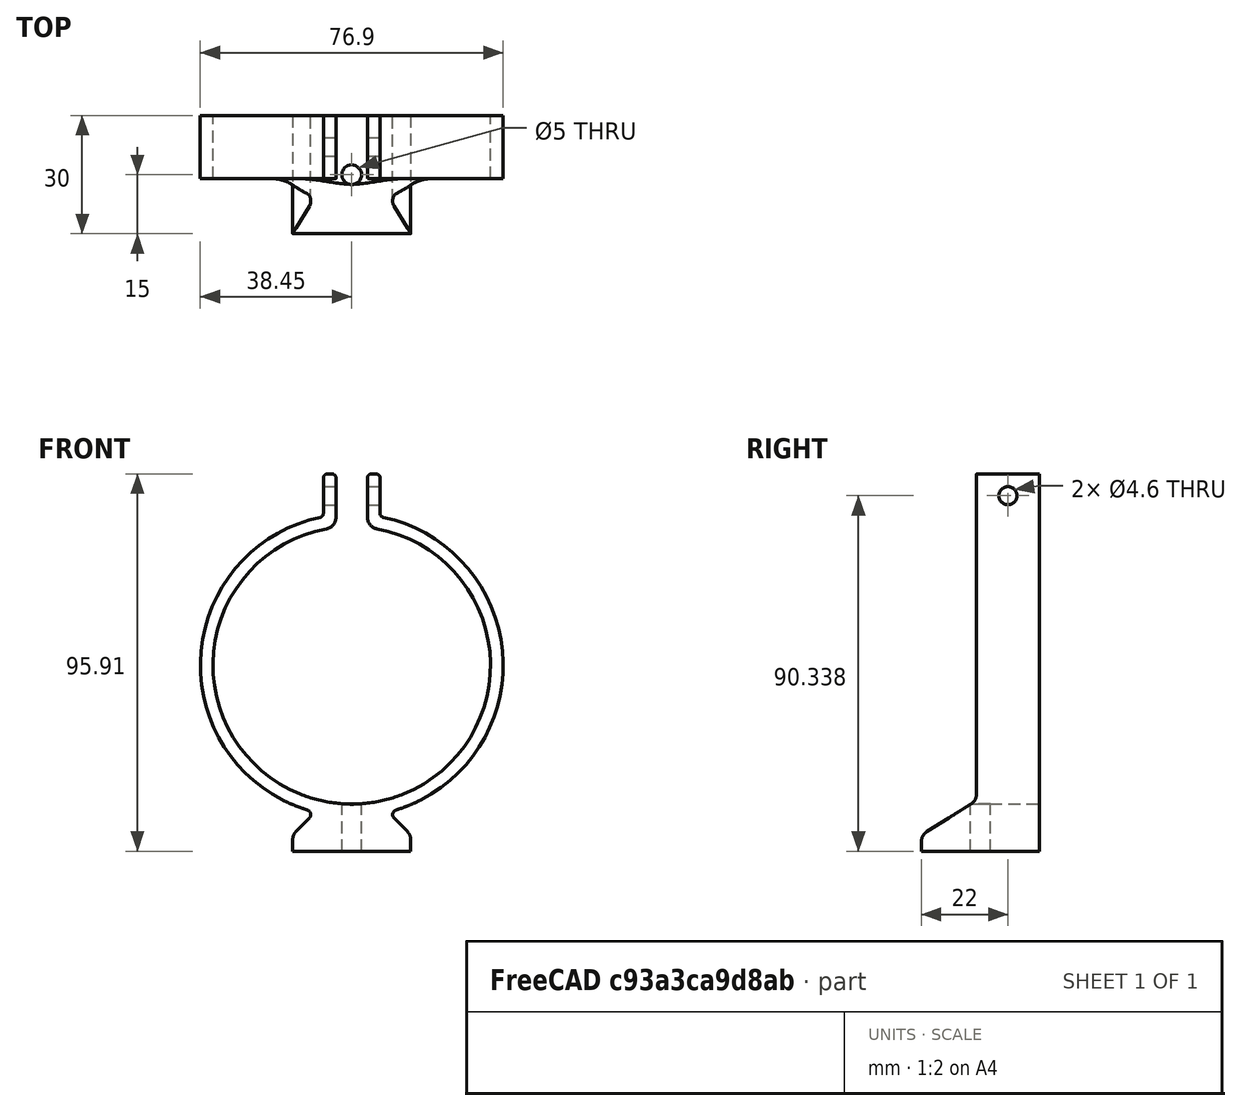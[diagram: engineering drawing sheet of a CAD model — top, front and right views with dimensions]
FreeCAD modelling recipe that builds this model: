
FCSTD DOCUMENT  (FreeCAD 1.0R39109 (Git))
Label: cam_lens_mt_v2
License: All rights reserved
LicenseURL: http://en.wikipedia.org/wiki/All_rights_reserved
objects: Sketcher::SketchObject×4, PartDesign::Pocket×2, Spreadsheet::Sheet×1, PartDesign::Pad×1, PartDesign::Hole×1, PartDesign::Body×1, App::Part×1, Mesh::Feature×1
note: 21 computed .brp shape members not serialized (recipe doc carries the construction recipe); baked Part::Feature solids carry a one-line shape summary decoded from their .brp

FEATURE [Spreadsheet::Sheet] Spreadsheet  label="pp"
  cells = A2='lens diam; B2(lens_diam)==70.5 mm; A3='ring width; B3(ring_width)==16 mm; A4='ring height above base; B4(ring_height_above_base)==12 mm; A5='ring tab height; B5(ring_tab_height)==9 mm; A6='ring tab hole diam; B6(ring_tab_hole)==4.6 mm; A7='ring gap; B7(ring_gap)==8 mm; A8='wall thick ring; B8(wall_thick_ring)==3.2 mm; A9='wall thick plate; B9(wall_thick)==5 mm; A10='plate width; B10(plate_width)==30 mm; A11='plate length; B11(plate_leng)==30 mm; A13='std rad; B13(std_rad)==3 mm; A14='std rad small; B14(std_rad_small)==1.6 mm
FEATURE [Sketcher::SketchObject] Sketch  label="Sketch_main"
  ArcFitTolerance = 0
  AttachmentSupport = -> [XZ_Plane001]
  FullyConstrained = true
  MakeInternals = false
  MapMode = 5
  Placement = pos=(0,0,0) rot=(1,0,0;1.5708rad)
  expr: Constraints[19] = <<pp>>.std_rad
  expr: Constraints[3] = <<pp>>.lens_diam + 2 * <<pp>>.wall_thick_ring
  expr: Constraints[54] = <<pp>>.wall_thick
  expr: Constraints[57] = <<pp>>.ring_height_above_base
  expr: Constraints[58] = <<pp>>.plate_width
  expr: Constraints[66] = <<pp>>.wall_thick_ring / 3
  expr: Constraints[68] = <<pp>>.lens_diam
  expr: Constraints[69] = <<pp>>.plate_width * 0.75
  expr: Constraints[74] = <<pp>>.wall_thick_ring
  expr: Constraints[75] = <<pp>>.ring_gap
  expr: Constraints[76] = <<pp>>.ring_tab_height
  sketch-geometry (32):
    g0: ArcOfCircle CenterX=0 CenterY=47.25 CenterZ=0 NormalX=0 NormalY=0 NormalZ=1 AngleXU=0 Radius=35.25 StartAngle=1.75484 EndAngle=7.66994
    g1: ArcOfCircle CenterX=0 CenterY=47.25 CenterZ=0 NormalX=0 NormalY=0 NormalZ=1 AngleXU=0 Radius=38.45 StartAngle=1.78155 EndAngle=4.41546
    g2: ArcOfCircle CenterX=0 CenterY=47.25 CenterZ=0 NormalX=0 NormalY=0 NormalZ=1 AngleXU=0 Radius=38.45 StartAngle=5.00932 EndAngle=7.6446
    g3: LineSegment StartX=-15 StartY=0 StartZ=0 EndX=15 EndY=0 EndZ=0
    g4: LineSegment StartX=-15 StartY=0 StartZ=0 EndX=-15 EndY=2.90664 EndZ=0
    g5: LineSegment StartX=15 StartY=0 StartZ=0 EndX=15 EndY=2.90664 EndZ=0
    g6: LineSegment [constr] StartX=-15 StartY=2.90664 StartZ=0 EndX=15 EndY=2.90664 EndZ=0
    g7: LineSegment StartX=-4 StartY=84.854 StartZ=0 EndX=-4 EndY=94.8384 EndZ=0
    g8: LineSegment StartX=4 StartY=84.854 StartZ=0 EndX=4 EndY=94.8384 EndZ=0
    g9: ArcOfCircle CenterX=-7 CenterY=84.854 CenterZ=0 NormalX=0 NormalY=0 NormalZ=1 AngleXU=0 Radius=3 StartAngle=4.89643 EndAngle=6.28319
    g10: ArcOfCircle CenterX=7 CenterY=84.854 CenterZ=0 NormalX=0 NormalY=0 NormalZ=1 AngleXU=0 Radius=3 StartAngle=3.14159 EndAngle=4.52835
    g11: LineSegment StartX=-7.2 StartY=85.8923 StartZ=0 EndX=-7.2 EndY=94.8384 EndZ=0
    g12: LineSegment StartX=-6.13333 StartY=95.905 StartZ=0 EndX=-5.06667 EndY=95.905 EndZ=0
    g13: LineSegment StartX=5.06667 StartY=95.905 StartZ=0 EndX=6.13333 EndY=95.905 EndZ=0
    g14: ArcOfCircle CenterX=-8.26667 CenterY=85.8923 CenterZ=0 NormalX=0 NormalY=0 NormalZ=1 AngleXU=0 Radius=1.06667 StartAngle=4.92314 EndAngle=6.28319
    g15: ArcOfCircle CenterX=8.2 CenterY=85.8384 CenterZ=0 NormalX=0 NormalY=0 NormalZ=1 AngleXU=0 Radius=1 StartAngle=3.14159 EndAngle=4.503
    g16: LineSegment [constr] StartX=-5.06667 StartY=95.905 StartZ=0 EndX=5.06667 EndY=95.905 EndZ=0
    g17: LineSegment [constr] StartX=-4 StartY=84.854 StartZ=0 EndX=4 EndY=84.854 EndZ=0
    g18: ArcOfCircle CenterX=-6.13333 CenterY=94.8384 CenterZ=0 NormalX=0 NormalY=0 NormalZ=1 AngleXU=0 Radius=1.06667 StartAngle=1.5708 EndAngle=3.14159
    g19: ArcOfCircle CenterX=-5.06667 CenterY=94.8384 CenterZ=0 NormalX=0 NormalY=0 NormalZ=1 AngleXU=0 Radius=1.06667 StartAngle=6.5e-15 EndAngle=1.5708
    g20: ArcOfCircle CenterX=5.06667 CenterY=94.8384 CenterZ=0 NormalX=0 NormalY=0 NormalZ=1 AngleXU=0 Radius=1.06667 StartAngle=1.5708 EndAngle=3.14159
    g21: ArcOfCircle CenterX=6.13333 CenterY=94.8384 CenterZ=0 NormalX=0 NormalY=0 NormalZ=1 AngleXU=0 Radius=1.06667 StartAngle=5.1e-15 EndAngle=1.5708
    g22: LineSegment StartX=-10.7415 StartY=8.49779 StartZ=0 EndX=-14.1489 EndY=5 EndZ=0
    g23: LineSegment StartX=10.7415 StartY=8.49779 StartZ=0 EndX=14.1489 EndY=5 EndZ=0
    g24: ArcOfCircle CenterX=-11.6011 CenterY=9.33514 CenterZ=0 NormalX=0 NormalY=0 NormalZ=1 AngleXU=0 Radius=1.2 StartAngle=5.51088 EndAngle=7.55705
    g25: ArcOfCircle CenterX=11.6011 CenterY=9.33514 CenterZ=0 NormalX=0 NormalY=0 NormalZ=1 AngleXU=0 Radius=1.2 StartAngle=1.86773 EndAngle=3.9139
    g26: ArcOfCircle CenterX=12 CenterY=2.90664 CenterZ=0 NormalX=0 NormalY=0 NormalZ=1 AngleXU=0 Radius=3 StartAngle=0 EndAngle=0.772305
    g27: ArcOfCircle CenterX=-12 CenterY=2.90664 CenterZ=0 NormalX=0 NormalY=0 NormalZ=1 AngleXU=0 Radius=3 StartAngle=2.36929 EndAngle=3.14159
    g28: GeomPoint [constr] X=0 Y=12 Z=0
    g29: GeomPoint [constr] X=7.2 Y=90.3384 Z=0
    g30: LineSegment [constr] StartX=-11.25 StartY=10.4826 StartZ=0 EndX=11.25 EndY=10.4826 EndZ=0
    g31: LineSegment StartX=7.2 StartY=85.8384 StartZ=0 EndX=7.2 EndY=94.8384 EndZ=0
  constraints (78):
    c: PointOnObject(g0,g-2)
    c: Coincident(g1,g0)
    c: Coincident(g2,g0)
    c: Diameter(g2) = 76.9
    c: Equal(g2,g1)
    c: Horizontal(g3)
    c: Symmetric(g3,g3,g-1)
    c: Coincident(g4,g3)
    c: Vertical(g4)
    c: Coincident(g5,g3)
    c: Vertical(g5)
    c: Horizontal(g6)
    c: Vertical(g7)
    c: Vertical(g8)
    c: Tangent(g7,g9) = -1.5708
    c: Tangent(g0,g9) = 1.5708
    c: Tangent(g0,g10) = 1.5708
    c: Tangent(g8,g10) = 1.5708
    c: Equal(g10,g9)
    c: Radius(g10) = 3
    c: Vertical(g11)
    c: Horizontal(g13)
    c: Horizontal(g12)
    c: Tangent(g11,g14) = -1.5708
    c: Tangent(g1,g14) = 1.5708
    c: Tangent(g2,g15) = 1.5708
    c: Radius(g15) = 1
    c: Coincident(g17,g7)
    c: Coincident(g17,g8)
    c: Horizontal(g16)
    c: Horizontal(g17)
    c: Equal(g13,g12)
    c: Tangent(g11,g18) = 1.5708
    c: Tangent(g12,g18) = 1.5708
    c: Tangent(g7,g19) = -1.5708
    c: Tangent(g12,g19) = 1.5708
    c: Tangent(g8,g20) = 1.5708
    c: Tangent(g13,g20) = 1.5708
    c: Tangent(g13,g21) = 1.5708
    c: Coincident(g16,g13)
    c: Coincident(g16,g12)
    c: Equal(g21,g20)
    c: Equal(g19,g20)
    c: Equal(g19,g18)
    c: Tangent(g1,g24) = 1.5708
    c: Tangent(g22,g24) = 1.5708
    c: Tangent(g2,g25) = 1.5708
    c: Tangent(g23,g25) = -1.5708
    c: Tangent(g5,g26) = -1.5708
    c: Tangent(g23,g26) = 1.5708
    c: Tangent(g22,g27) = -1.5708
    c: Tangent(g4,g27) = 1.5708
    c: Coincident(g6,g4)
    c: Coincident(g6,g5)
    c: DistanceY(g3,g23) = 5
    c: PointOnObject(g28,g-2)
    c: PointOnObject(g28,g0)
    c: DistanceY(g-1,g28) = 12
    c: DistanceX(g3,g3) = 30
    c: DistanceY(g-1,g29) = 90.3384  'pp_ring_hole_height'
    c: Radius(g25) = 1.2
    c: Equal(g25,g24)
    c: Coincident(g30,g1)
    c: Coincident(g30,g2)
    c: Horizontal(g30)
    c: Radius(g26) = 3
    c: Radius(g21) = 1.06667
    c: Equal(g14,g18)
    c: Diameter(g0) = 70.5
    c: DistanceX(g30,g30) = 22.5
    c: Equal(g26,g27)
    c: Tangent(g31,g21) = -1.5708
    c: Tangent(g31,g15) = 1.5708
    c: Vertical(g31)
    c: DistanceX(g8,g21) = 3.2
    c: DistanceX(g17,g17) = 8
    c: DistanceY(g31,g31) = 9
    c: Symmetric(g15,g21,g29)
FEATURE [PartDesign::Pad] Pad  label="Pad_MainExt"
  Direction = (0,-1,-2e-16)
  Length = 30
  Length2 = 10
  Placement = pos=(0,0,0) rot=(1,0,0;1.5708rad)
  Profile = -> Sketch
  Suppressed = false
  Type = 0
  expr: Length = <<pp>>.plate_leng
FEATURE [Sketcher::SketchObject] Sketch001
  ArcFitTolerance = 0
  AttachmentSupport = -> [YZ_Plane001]
  FullyConstrained = true
  MakeInternals = false
  MapMode = 5
  Placement = pos=(0,0,0) rot=(0.57735,0.57735,0.57735;2.0944rad)
  expr: Constraints[14] = <<pp>>.std_rad
  expr: Constraints[16] = <<pp>>.wall_thick
  expr: Constraints[17] = <<pp>>.ring_height_above_base
  expr: Constraints[18] = <<pp>>.ring_width
  expr: Constraints[19] = <<pp>>.lens_diam * 1.5
  expr: Constraints[21] = <<pp>>.plate_leng
  sketch-geometry (8):
    g0: LineSegment StartX=-16 StartY=120.293 StartZ=0 EndX=-16 EndY=14.5429 EndZ=0
    g1: LineSegment StartX=-17.4083 StartY=12 StartZ=0 EndX=-28.5917 EndY=5 EndZ=0
    g2: LineSegment StartX=-121.75 StartY=0 StartZ=0 EndX=-121.75 EndY=120.293 EndZ=0
    g3: LineSegment StartX=-121.75 StartY=120.293 StartZ=0 EndX=-16 EndY=120.293 EndZ=0
    g4: LineSegment StartX=-30 StartY=2.45707 StartZ=0 EndX=-30 EndY=3.322e-13 EndZ=0
    g5: LineSegment StartX=-30 StartY=3.322e-13 StartZ=0 EndX=-121.75 EndY=0 EndZ=0
    g6: ArcOfCircle CenterX=-19 CenterY=14.5429 CenterZ=0 NormalX=0 NormalY=0 NormalZ=1 AngleXU=0 Radius=3 StartAngle=5.27166 EndAngle=6.28319
    g7: ArcOfCircle CenterX=-27 CenterY=2.45707 CenterZ=0 NormalX=0 NormalY=0 NormalZ=1 AngleXU=0 Radius=3 StartAngle=2.13006 EndAngle=3.14159
  constraints (22):
    c: Vertical(g0)
    c: Vertical(g2)
    c: Coincident(g3,g2)
    c: Coincident(g3,g0)
    c: Horizontal(g3)
    c: PointOnObject(g4,g-1)
    c: Vertical(g4)
    c: Coincident(g5,g4)
    c: PointOnObject(g5,g-1)
    c: Coincident(g2,g5)
    c: Tangent(g1,g6) = 1.5708
    c: Tangent(g0,g6) = 1.5708
    c: Tangent(g1,g7) = -1.5708
    c: Tangent(g4,g7) = -1.5708
    c: Radius(g6) = 3
    c: Equal(g6,g7)
    c: DistanceY(g4,g1) = 5
    c: DistanceY(g-1,g1) = 12
    c: DistanceX(g0,g-1) = 16
    c: DistanceY(g0,g0) = 105.75
    c: Equal(g0,g3)
    c: DistanceX(g4,g-1) = 30
FEATURE [PartDesign::Pocket] Pocket  label="Pocket_SculptPlate"
  BaseFeature = -> Pad
  Direction = (1,1,1)
  Length = 5
  Length2 = 5
  Midplane = true
  Placement = pos=(0,0,0) rot=(1,0,0;1.5708rad)
  Profile = -> Sketch001
  Suppressed = false
  Type = 1
FEATURE [Sketcher::SketchObject] Sketch002
  ArcFitTolerance = 0
  AttachmentSupport = -> [XY_Plane001]
  FullyConstrained = true
  MakeInternals = false
  MapMode = 5
  expr: Constraints[2] = <<pp>>.plate_leng / 2
  sketch-geometry (1):
    g0: Circle CenterX=0 CenterY=-15 CenterZ=0 NormalX=0 NormalY=0 NormalZ=1 AngleXU=0 Radius=5
  constraints (3):
    c: PointOnObject(g0,g-2)
    c: Diameter(g0) = 10
    c: DistanceY(g0,g-1) = 15
FEATURE [PartDesign::Hole] Hole  label="Hole_M6"
  BaseFeature = -> Pocket
  CustomThreadClearance = 0
  Depth = 30
  DepthType = 0
  Diameter = 5
  DrillForDepth = false
  DrillPoint = 1
  DrillPointAngle = 118
  HoleCutCountersinkAngle = 90
  HoleCutCustomValues = false
  HoleCutDepth = 0
  HoleCutDiameter = 5.1
  HoleCutType = 0
  ModelThread = false
  Placement = pos=(0,0,0) rot=(1,0,0;1.5708rad)
  Profile = -> Sketch002
  Reversed = true
  Suppressed = false
  Tapered = false
  TaperedAngle = 90
  ThreadClass = 0
  ThreadDepth = 23.5
  ThreadDepthType = 0
  ThreadDirection = 0
  ThreadFit = 0
  ThreadSize = 14
  ThreadType = 1
  Threaded = true
  UseCustomThreadClearance = false
FEATURE [Sketcher::SketchObject] Sketch003
  ArcFitTolerance = 0
  AttachmentSupport = -> [YZ_Plane001]
  FullyConstrained = true
  MakeInternals = false
  MapMode = 5
  Placement = pos=(0,0,0) rot=(0.57735,0.57735,0.57735;2.0944rad)
  expr: Constraints[0] = <<pp>>.ring_width / 2
  expr: Constraints[1] = <<pp>>.ring_tab_hole
  expr: Constraints[2] = Sketch.Constraints.pp_ring_hole_height
  sketch-geometry (1):
    g0: Circle CenterX=-8 CenterY=90.3384 CenterZ=0 NormalX=0 NormalY=0 NormalZ=1 AngleXU=0 Radius=2.3
  constraints (3):
    c: DistanceX(g0,g-1) = 8
    c: Diameter(g0) = 4.6
    c: DistanceY(g-1,g0) = 90.3384
FEATURE [PartDesign::Pocket] Pocket001
  BaseFeature = -> Hole
  Direction = (1,1,1)
  Length = 5
  Length2 = 5
  Midplane = true
  Placement = pos=(0,0,0) rot=(1,0,0;1.5708rad)
  Profile = -> Sketch003
  Suppressed = false
  Type = 1
FEATURE [PartDesign::Body] Body  label="cam_lens_mt_M6"
  AllowCompound = false
  Group = -> [Sketch,Pad,Sketch001,Pocket,Sketch002,Hole,Sketch003,Pocket001]
  Origin = -> Origin001
  Tip = -> Pocket001
FEATURE [App::Part] Part  label="cam_lens_mt_part"
  Group = -> [Body]
  Origin = -> Origin
FEATURE [Mesh::Feature] Mesh  label="cam_lens_mt_M6 (Meshed)"
